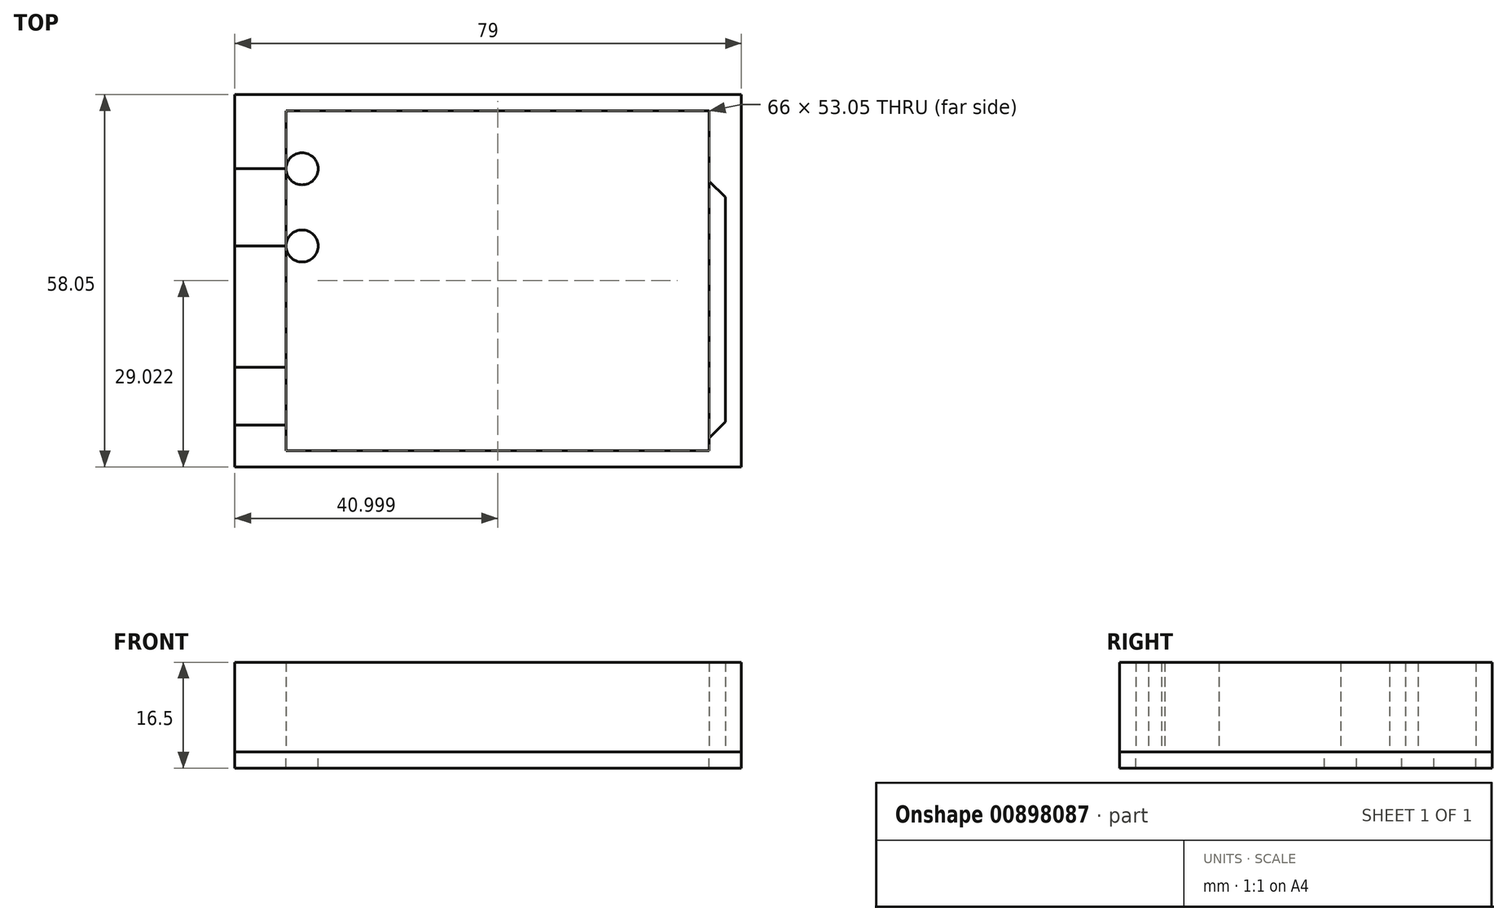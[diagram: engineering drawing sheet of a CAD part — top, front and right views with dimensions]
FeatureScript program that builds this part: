
annotation { "Feature Type Name" : "Feature", "Feature Type Description" : "" }
export const myFeature = defineFeature(function(context is Context, id is Id, definition is map)
    precondition{}
    {
        {
            var Q0;
            Q0=qCreatedBy(makeId("Top.planeOp"),FACE);
            var sketch = newSketch(context, id + "F0", { "sketchPlane" : qUnion([Q0])});
            skLineSegment(sketch, "E0.bottom", {"start": v(-51.17, 26.59) * mm, "end": v(17.33, 26.59) * mm});
            skLineSegment(sketch, "E0.top", {"start": v(-51.17, -26.46) * mm, "end": v(17.33, -26.46) * mm});
            skLineSegment(sketch, "E0.left", {"start": v(-51.17, 26.59) * mm, "end": v(-51.17, -26.46) * mm});
            skLineSegment(sketch, "E0.right", {"start": v(17.33, 26.59) * mm, "end": v(17.33, -26.46) * mm});
            skLineSegment(sketch, "E1.bottom", {"start": v(-51.17, 26.59) * mm, "end": v(14.83, 26.59) * mm});
            skLineSegment(sketch, "E1.top", {"start": v(-51.17, -26.46) * mm, "end": v(14.83, -26.46) * mm});
            skLineSegment(sketch, "E1.right", {"start": v(14.83, 26.59) * mm, "end": v(14.83, -26.46) * mm});
            skPoint(sketch, "E2", {"position": v(14.83, 15.59) * mm});
            skPoint(sketch, "E3", {"position": v(14.83, -24.46) * mm});
            skLineSegment(sketch, "E4", {"start": v(14.83, 15.59) * mm, "end": v(17.33, 13.09) * mm});
            skLineSegment(sketch, "E5", {"start": v(14.83, -24.46) * mm, "end": v(17.33, -21.96) * mm});
            skLineSegment(sketch, "E6.bottom", {"start": v(-59.17, 29.09) * mm, "end": v(19.83, 29.09) * mm});
            skLineSegment(sketch, "E6.top", {"start": v(-59.17, -28.96) * mm, "end": v(19.83, -28.96) * mm});
            skLineSegment(sketch, "E6.left", {"start": v(-59.17, 29.09) * mm, "end": v(-59.17, -28.96) * mm});
            skLineSegment(sketch, "E6.right", {"start": v(19.83, 29.09) * mm, "end": v(19.83, -28.96) * mm});
            skLineSegment(sketch, "E7.bottom", {"start": v(-59.17, 17.54) * mm, "end": v(-51.17, 17.54) * mm});
            skLineSegment(sketch, "E7.top", {"start": v(-59.17, 5.49) * mm, "end": v(-51.17, 5.49) * mm});
            skLineSegment(sketch, "E7.left", {"start": v(-59.17, 17.54) * mm, "end": v(-59.17, 5.49) * mm});
            skLineSegment(sketch, "E7.right", {"start": v(-51.17, 17.54) * mm, "end": v(-51.17, 5.49) * mm});
            skLineSegment(sketch, "E8.bottom", {"start": v(-59.17, -13.46) * mm, "end": v(-51.17, -13.46) * mm});
            skLineSegment(sketch, "E8.top", {"start": v(-59.17, -22.46) * mm, "end": v(-51.17, -22.46) * mm});
            skLineSegment(sketch, "E8.left", {"start": v(-59.17, -13.46) * mm, "end": v(-59.17, -22.46) * mm});
            skLineSegment(sketch, "E8.right", {"start": v(-51.17, -13.46) * mm, "end": v(-51.17, -22.46) * mm});
            skLineSegment(sketch, "E9.bottom", {"start": v(-51.17, 17.54) * mm, "end": v(-48.67, 17.54) * mm});
            skLineSegment(sketch, "E9.top", {"start": v(-51.17, 5.49) * mm, "end": v(-48.67, 5.49) * mm});
            skLineSegment(sketch, "E9.right", {"start": v(-48.67, 17.54) * mm, "end": v(-48.67, 5.49) * mm});
            skCircle(sketch, "E10", {"center": v(-48.67, 17.54) * mm, "radius": 2.5 * mm});
            skCircle(sketch, "E11", {"center": v(-48.67, 5.49) * mm, "radius": 2.5 * mm});
            skSolve(sketch);
        }
        {
            var Q0;
            {var subQ9=sQuery(id+"F0.wireOp",EDGE,"E0.bottom");Q0=makeQuery(id+"F0.imprint","IMPRINT",FACE,{"disambiguationData":[TD([[makeQuery(id+"F0.imprint","IMPRINT",EDGE,{"derivedFrom":subQ9}),1.0]])]});}
            var Q1;
            {var subQ0=sQuery(id+"F0.wireOp",EDGE,"E7.top");Q1=makeQuery(id+"F0.imprint","IMPRINT",FACE,{"disambiguationData":[TD([[makeQuery(id+"F0.imprint","IMPRINT",EDGE,{"derivedFrom":subQ0}),-1.0]])]});}
            var Q2;
            {var subQ0=sQuery(id+"F0.wireOp",EDGE,"E0.bottom");Q2=makeQuery(id+"F0.imprint","IMPRINT",FACE,{"disambiguationData":[TD([[makeQuery(id+"F0.imprint","IMPRINT",EDGE,{"derivedFrom":subQ0}),-1.0]])]});}
            var Q3;
            {var subQ0=sQuery(id+"F0.wireOp",EDGE,"E0.top");Q3=makeQuery(id+"F0.imprint","IMPRINT",FACE,{"disambiguationData":[TD([[makeQuery(id+"F0.imprint","IMPRINT",EDGE,{"derivedFrom":subQ0}),1.0]])]});}
            extrude(context, id + "F1", {"entities" : qUnion([Q0, Q1, Q2, Q3]), "depth" : 14 * mm, "offsetDistance" : 25 * mm});
        }
        {
            var Q0;
            {var subQ3=sQuery(id+"F0.wireOp",EDGE,"E1.bottom");Q0=makeQuery(id+"F0.imprint","IMPRINT",FACE,{"disambiguationData":[TD([[makeQuery(id+"F0.imprint","IMPRINT",EDGE,{"derivedFrom":subQ3}),-1.0]])]});}
            var Q1;
            Q1=makeQuery(id+"F0.imprint","IMPRINT",FACE,{"disambiguationData":[TD([[makeQuery(id+"F0.imprint","IMPRINT",EDGE,{"derivedFrom":sQuery(id+"F0.wireOp",EDGE,"E8.bottom")}),-1.0]])]});
            var Q2;
            {var subQ9=sQuery(id+"F0.wireOp",EDGE,"E0.bottom");Q2=makeQuery(id+"F0.imprint","IMPRINT",FACE,{"disambiguationData":[TD([[makeQuery(id+"F0.imprint","IMPRINT",EDGE,{"derivedFrom":subQ9}),1.0]])]});}
            var Q3;
            {var subQ0=sQuery(id+"F0.wireOp",EDGE,"E7.top");Q3=makeQuery(id+"F0.imprint","IMPRINT",FACE,{"disambiguationData":[TD([[makeQuery(id+"F0.imprint","IMPRINT",EDGE,{"derivedFrom":subQ0}),-1.0]])]});}
            var Q4;
            Q4=makeQuery(id+"F0.imprint","IMPRINT",FACE,{"disambiguationData":[TD([[makeQuery(id+"F0.imprint","IMPRINT",EDGE,{"derivedFrom":sQuery(id+"F0.wireOp",EDGE,"E7.bottom")}),-1.0]])]});
            var Q5;
            {var subQ0=sQuery(id+"F0.wireOp",EDGE,"E4");Q5=makeQuery(id+"F0.imprint","IMPRINT",FACE,{"disambiguationData":[TD([[makeQuery(id+"F0.imprint","IMPRINT",EDGE,{"derivedFrom":subQ0}),-1.0]])]});}
            var Q6;
            {var subQ0=sQuery(id+"F0.wireOp",EDGE,"E0.top");Q6=makeQuery(id+"F0.imprint","IMPRINT",FACE,{"disambiguationData":[TD([[makeQuery(id+"F0.imprint","IMPRINT",EDGE,{"derivedFrom":subQ0}),1.0]])]});}
            var Q7;
            {var subQ0=sQuery(id+"F0.wireOp",EDGE,"E0.bottom");Q7=makeQuery(id+"F0.imprint","IMPRINT",FACE,{"disambiguationData":[TD([[makeQuery(id+"F0.imprint","IMPRINT",EDGE,{"derivedFrom":subQ0}),-1.0]])]});}
            var Q8;
            {var subQ0=sQuery(id+"F0.wireOp",EDGE,"E9.bottom");Q8=makeQuery(id+"F0.imprint","IMPRINT",FACE,{"disambiguationData":[TD([[makeQuery(id+"F0.imprint","IMPRINT",EDGE,{"derivedFrom":subQ0}),1.0]])]});}
            var Q9;
            {var subQ0=sQuery(id+"F0.wireOp",EDGE,"E9.bottom");Q9=makeQuery(id+"F0.imprint","IMPRINT",FACE,{"disambiguationData":[TD([[makeQuery(id+"F0.imprint","IMPRINT",EDGE,{"derivedFrom":subQ0}),-1.0]])]});}
            var Q10;
            {var subQ0=sQuery(id+"F0.wireOp",EDGE,"E7.right");Q10=makeQuery(id+"F0.imprint","IMPRINT",FACE,{"disambiguationData":[TD([[makeQuery(id+"F0.imprint","IMPRINT",EDGE,{"derivedFrom":subQ0}),1.0]])]});}
            var Q11;
            {var subQ0=sQuery(id+"F0.wireOp",EDGE,"E9.top");Q11=makeQuery(id+"F0.imprint","IMPRINT",FACE,{"disambiguationData":[TD([[makeQuery(id+"F0.imprint","IMPRINT",EDGE,{"derivedFrom":subQ0}),1.0]])]});}
            var Q12;
            {var subQ0=sQuery(id+"F0.wireOp",EDGE,"E9.top");Q12=makeQuery(id+"F0.imprint","IMPRINT",FACE,{"disambiguationData":[TD([[makeQuery(id+"F0.imprint","IMPRINT",EDGE,{"derivedFrom":subQ0}),-1.0]])]});}
            extrude(context, id + "F2", {"entities" : qUnion([Q0, Q1, Q2, Q3, Q4, Q5, Q6, Q7, Q8, Q9, Q10, Q11, Q12]), "depth" : -2.5 * mm, "offsetDistance" : 25 * mm});
        }
    });
